# Revit family: JOMA_Littera_Vinkel_Förstärkningsbricka
name_source: partatom
category: Structural Connection Tags
revit_build: Autodesk Revit 2017 (Build: 20171027_0315(x64)
units: mm (PartAtom-declared; Revit-internal decimal feet)

## family parameters
Rotate with component = Yes

## types (6) — shared parameters

## per-type parameters (varying)
| type | Förstärkningsbricka enkel bultinföstning |
| Enkel spikinfästning | No |
| Dubbel spikinfästning | No |
| Enkel bultinfästning | Yes |
| Dubbel bultinfästning | No |
| Genomgående bultinfästning | No |
| Förstärkningsbricka enkel bultinfästning | Yes |

type visibility flags (boolean, named after types; folded from table):
- Enkel spikinfästning: Yes: Enkel spikinfästning
- Dubbel spikinfästning: Yes: Dubbel spikinfästning
- Enkel bultinfästning: Yes: Enkel bultinfästning
- Dubbel bultinfästning: Yes: Dubbel bultinfästning
- Genomgående bultinfästning: Yes: Genomgående bultinfästning
- Förstärkningsbricka enkel bultinfästning: Yes: (none)
